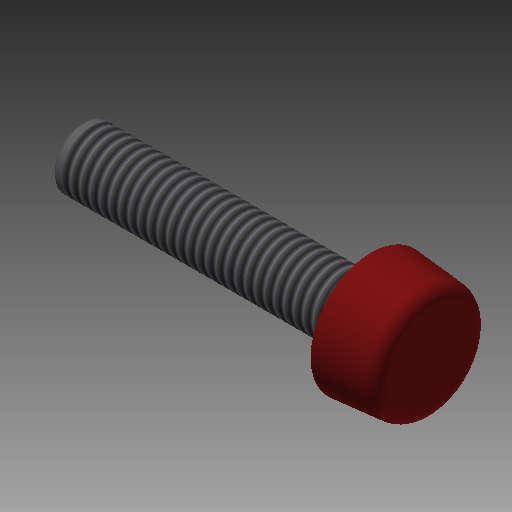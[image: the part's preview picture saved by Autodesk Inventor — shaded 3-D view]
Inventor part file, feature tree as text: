
AUTODESK INVENTOR PART (.ipt)
format: ipt  version: 2018 (Build 220112000, 112)  size: 156,672 bytes
history: native  units: mm
features: other x7, revolve x1, thread x1, sketch x1
ambient origin geometry x8: Origin, YZ Plane, XZ Plane, XY Plane, X Axis, Y Axis, Z Axis, Center Point
bodies: Solid1 (feature_tree)
feature tree (10):
  revolve  "Revolution1"  [1 undecoded]
  thread  "Thread1"  [1 undecoded]
  other  "AS_XY"
  other  "AS_YZ"
  other  "AS_ZX"
  other  "AS_X"
  other  "AS_Y"
  other  "AS_Z"
  other  "AS_Center"
  sketch  "Skizze_1"  dims[d0=360.0deg d1=23.5mm d2=0.5mm]
note: 2 required parameter values undecoded (feature->parameter linkage not recoverable at this tier; creation-order binding heuristic only, values carry confidence <= 0.55)